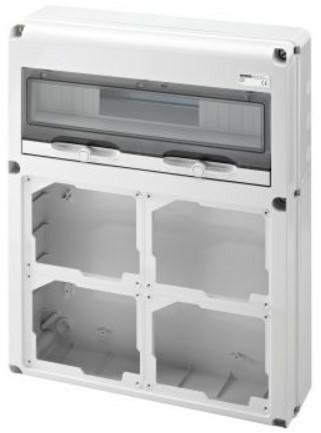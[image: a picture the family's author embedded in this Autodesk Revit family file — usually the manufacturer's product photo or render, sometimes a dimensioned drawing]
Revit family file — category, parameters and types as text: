
# Revit family: Building-QuadriIEC309-GEWISS-68QDIN-QUADRI-PRESE-20MOD_4PRESE_IB_ORIZ
name_source: partatom
category: Apparecchi elettrici
units: mm (PartAtom-declared; Revit-internal decimal feet)

## family parameters
Condiviso = No
Host = Superficie
Mantenere orientamento annotazione = Sì
Punto di calcolo locali = Sì
Quota connettore circolare = Usa diametro
Taglio con vuoti quando caricato = No
Tipo di parte = Normale

## types (1)
- GW68014N - Q-DIN 20M 4FLANGE PR.BL.OR.CBF IP65
    Catalogo = BUILDING
    Catalogo Serie = 68 QDIN
    Classe isolamento = II
    Codice EAN = 8011564744837
    Codice Electrocod = 2242
    Colore = Grigio RAL 7035
    Conformità normativa = EN 60208 - EN 60670-1 - IEC 60670-24
    Descrizione = Q-DIN 20M 4FLANGE PR.BL.OR.CBF IP65
    Glow Wire Test = 650°C
    Grado di protezione = IP65
    IDF = 6d7a8f00-70f4-417a-94c1-695c300c42a1
    IDT = 90d6f30b-0b77-4e9c-bb41-47f43079aa94
    Immagine tipo = GW68014N.jpg
    Modello = GW68014N
    N. IEC 309/IB alloggiabili = 4 IB Orizz. 16/32 A CBF IP44
    N. coperchi ciechi in dotazione = 2 IB 16/32 A
    N. flange in dotazione = 2 IB 16/32 A
    N. mod. EN 50022 = 20
    N. prese IB alloggiabili: = 4 IB Orizz. 16/32 A CBF IP44
    N. prese alloggiabili = 4 IB Orizz. 16/32 A CBF IP44
    POMELLO = bianco
    PRESA = rosso
    Per prese: = Orizzontali CBF
    Potenza dissipabile A (W) = 30
    Potenza dissipabile B (W) = 92
    Produttore = GEWISS S.p.A.
    Prospetto di default = 1219 mm
    Resistenza agli urti = IK08
    SEO = Quadretto
    STRUTTURA = RAL - 7035
    STRUTTURA ALTA = Poche
    Scheda Tecnica = https://www.gewiss.com
    Spostamento_S = 1000 mm  [stored 3.28084 ft]
    Temperatura di funzionamento = -25 ÷ +40 °C
    Temperatura di utilizzo = -25 +40 °C
    Termopressione con biglia = 70 °C
    Tipo versione = Vuoto
    Tipologia di installazione = Da parete
    URL = https://www.gewiss.com
    VETRO = Vetro
    Versione file RFA = 21.5

note: [stored X ft] marks values corroborated as IEEE doubles in the binary element streams (Revit-internal decimal feet)

## geometry (parser evidence)
native form markers: Sweep x3
no freeform markers — native parametric forms only
